# Revit family: FP-Revit20-en-WB24SMB1-WarmingDrawer-0-90003701-US-CA
name_source: partatom
category: Generic Models
units: mm (PartAtom-declared; Revit-internal decimal feet)

## family parameters
Always vertical = Yes
Can host rebar = No
Cut with Voids When Loaded = No
Part Type = Normal
Room Calculation Point = No
Round Connector Dimension = Use Diameter
Shared = No
Work Plane-Based = No

## types (1)
- WB24SMB1
    Cavity - Minimum Depth = 550 mm
    Cavity - Minimum Height = 142 mm  [stored 0.465879 ft]
    Cavity - Minimum width = 560 mm  [stored 1.83727 ft]
    Chassis - Depth = 546 mm  [stored 1.79134 ft]
    Chassis - Depth (including power plug, excluding flange) = 547 mm  [stored 1.79462 ft]
    Chassis - width = 543 mm  [stored 1.7815 ft]
    Connector note electrical = 220 - 240 V, 50 Hz, 10A
    Default Elevation = 0 mm  [stored 0 ft]
    Description = Warming Drawer, 24"
    Manufacturer = Fisher & Paykel Appliances
    Material - Chassis = Fisher & Paykel - Aluminium
    Material - Glass = Fisher & Paykel - Glass, Black
    Model = WB24SMB1
    Product - Overall Height = 140 mm  [stored 0.459318 ft]
    Product - Overall width = 596 mm  [stored 1.95538 ft]
    URL = www.fisherpaykel.com

note: [stored X ft] marks values corroborated as IEEE doubles in the binary element streams (Revit-internal decimal feet)

## geometry (parser evidence)
native form markers: Sweep x2
no freeform markers — native parametric forms only
